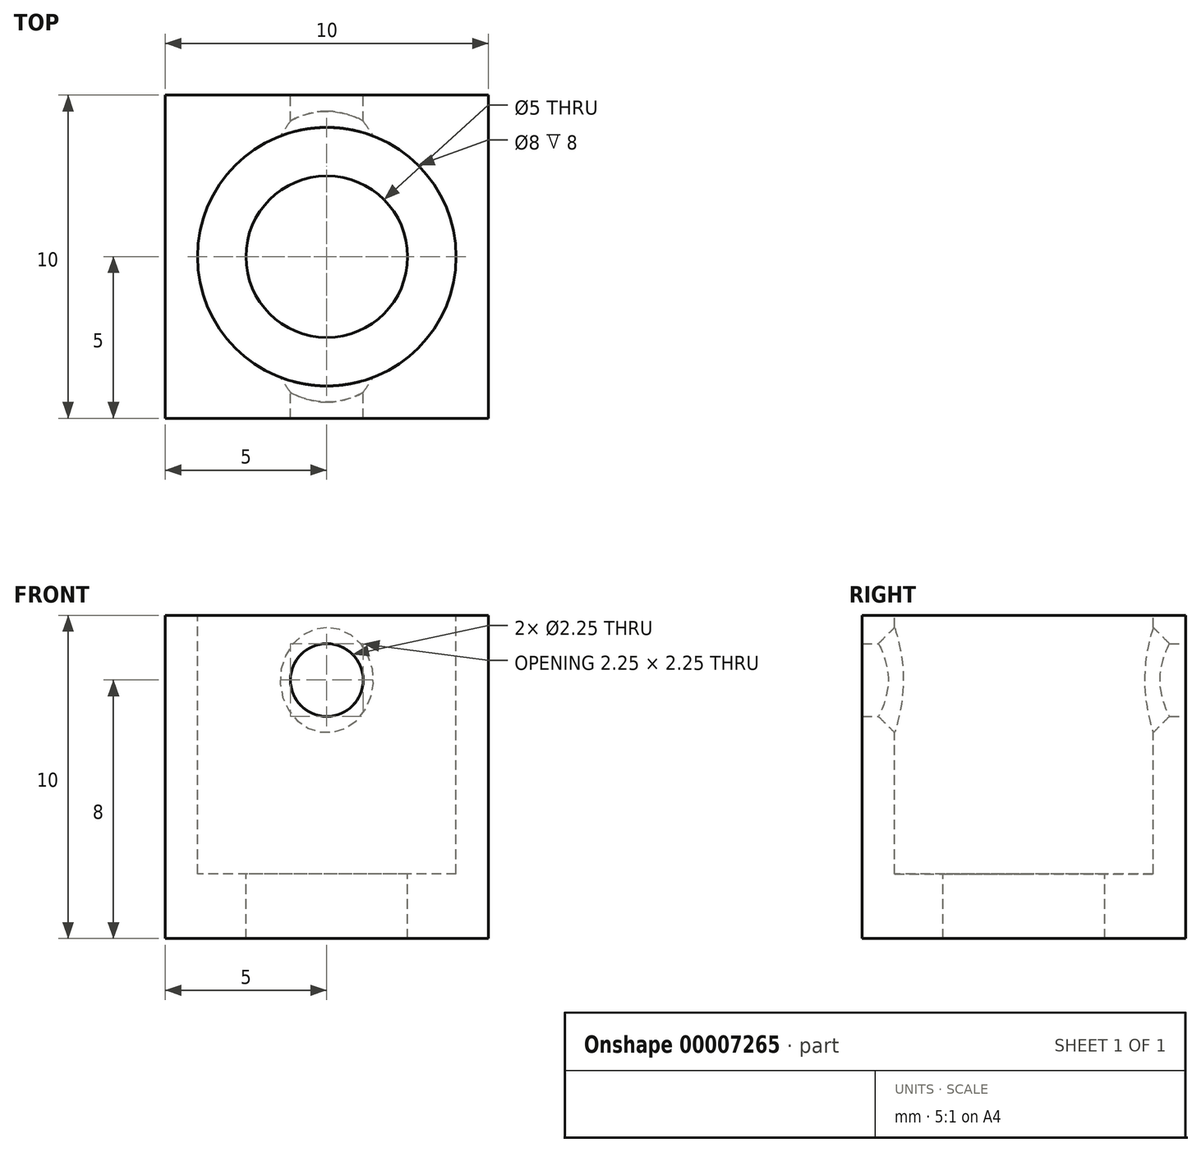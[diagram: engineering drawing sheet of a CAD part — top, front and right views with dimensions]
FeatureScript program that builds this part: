
annotation { "Feature Type Name" : "Feature", "Feature Type Description" : "" }
export const myFeature = defineFeature(function(context is Context, id is Id, definition is map)
    precondition{}
    {
        {
            var Q0;
            Q0=qCreatedBy(makeId("Front.planeOp"),FACE);
            var sketch = newSketch(context, id + "F0", { "sketchPlane" : qUnion([Q0])});
            skLineSegment(sketch, "E0.rect.bottom", {"start": v(5, -5) * mm, "end": v(-5, -5) * mm});
            skLineSegment(sketch, "E0.rect.top", {"start": v(5, 5) * mm, "end": v(-5, 5) * mm});
            skLineSegment(sketch, "E0.rect.left", {"start": v(5, -5) * mm, "end": v(5, 5) * mm});
            skLineSegment(sketch, "E0.rect.right", {"start": v(-5, -5) * mm, "end": v(-5, 5) * mm});
            skPoint(sketch, "E0.rect.middle", {"position": v(0, 0) * mm});
            skCircle(sketch, "E1", {"center": v(0, 3) * mm, "radius": 1.13 * mm});
            skSolve(sketch);
        }
        {
            var Q0;
            Q0 = qSketchRegion(id + "F0", true);
            extrude(context, id + "F1", {"entities" : qUnion([Q0]), "depth" : 10 * mm});
        }
        {
            var Q0;
            Q0=makeQuery(id+"F1.opExtrude","SWEPT_FACE",FACE,{"disambiguationData":[OSD([sQuery(id+"F0.wireOp",EDGE,"E0.rect.top")])]});
            var sketch = newSketch(context, id + "F2", { "sketchPlane" : qUnion([Q0])});
            skLineSegment(sketch, "E2", {"start": v(-5, 0) * mm, "end": v(5, -10) * mm, "construction": true});
            skCircle(sketch, "E3", {"center": v(0, -5) * mm, "radius": 2.5 * mm});
            skSolve(sketch);
        }
        {
            var Q0;
            Q0 = qSketchRegion(id + "F2", true);
            extrude(context, id + "F3", {"entities" : qUnion([Q0]), "operationType" : NewBodyOperationType.REMOVE, "oppositeDirection" : true, "depth" : 25 * mm});
        }
        {
            var Q0;
            Q0=makeQuery(id+"F1.opExtrude","SWEPT_FACE",FACE,{"disambiguationData":[OSD([sQuery(id+"F0.wireOp",EDGE,"E0.rect.top")])]});
            var sketch = newSketch(context, id + "F4", { "sketchPlane" : qUnion([Q0])});
            skCircle(sketch, "E4", {"center": v(0, -5) * mm, "radius": 4 * mm});
            skSolve(sketch);
        }
        {
            var Q0;
            Q0 = qSketchRegion(id + "F4", true);
            extrude(context, id + "F5", {"entities" : qUnion([Q0]), "operationType" : NewBodyOperationType.REMOVE, "oppositeDirection" : true, "depth" : 8 * mm});
        }
        {
            var Q0;
            {var subQ0=sQuery(id+"F0.wireOp",EDGE,"E1");Q0=makeQuery(id+"F5.boolean.opBoolean","INTERSECT",EDGE,{"derivedFrom":[makeQuery(id+"F3.boolean.opBoolean","SPLIT",FACE,{"disambiguationData":[TD([makeQuery(id+"F1.opExtrude","CAP_FACE",FACE,{"disambiguationData":[OSD([sQuery(id+"F0.wireOp",EDGE,"E0.rect.bottom"),sQuery(id+"F0.wireOp",EDGE,"E0.rect.top"),sQuery(id+"F0.wireOp",EDGE,"E0.rect.left"),sQuery(id+"F0.wireOp",EDGE,"E0.rect.right"),subQ0])],"isStart":true})])],"derivedFrom":makeQuery(id+"F1.opExtrude","SWEPT_FACE",FACE,{"disambiguationData":[OSD([subQ0])]})}),makeQuery(id+"F5.opExtrude","SWEPT_FACE",FACE,{"disambiguationData":[OSD([sQuery(id+"F4.wireOp",EDGE,"E4")])]})]});}
            var Q1;
            {var subQ0=sQuery(id+"F0.wireOp",EDGE,"E1");Q1=makeQuery(id+"F5.boolean.opBoolean","INTERSECT",EDGE,{"derivedFrom":[makeQuery(id+"F3.boolean.opBoolean","SPLIT",FACE,{"disambiguationData":[TD([makeQuery(id+"F1.opExtrude","CAP_FACE",FACE,{"disambiguationData":[OSD([sQuery(id+"F0.wireOp",EDGE,"E0.rect.bottom"),sQuery(id+"F0.wireOp",EDGE,"E0.rect.top"),sQuery(id+"F0.wireOp",EDGE,"E0.rect.left"),sQuery(id+"F0.wireOp",EDGE,"E0.rect.right"),subQ0])],"isStart":false})])],"derivedFrom":makeQuery(id+"F1.opExtrude","SWEPT_FACE",FACE,{"disambiguationData":[OSD([subQ0])]})}),makeQuery(id+"F5.opExtrude","SWEPT_FACE",FACE,{"disambiguationData":[OSD([sQuery(id+"F4.wireOp",EDGE,"E4")])]})]});}
            chamfer(context, id + "F6", {"entities" : qUnion([Q0, Q1]), "width" : .5 * mm, "tangentPropagation" : true});
        }
    });
